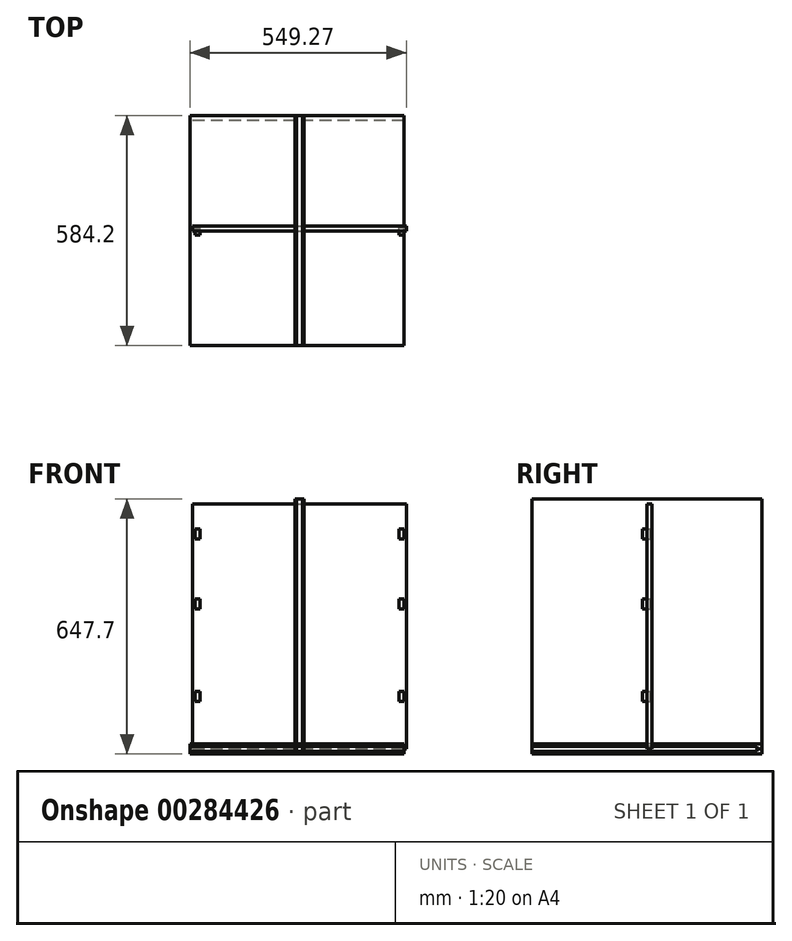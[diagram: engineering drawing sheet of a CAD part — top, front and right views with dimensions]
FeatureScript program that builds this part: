
annotation { "Feature Type Name" : "Feature", "Feature Type Description" : "" }
export const myFeature = defineFeature(function(context is Context, id is Id, definition is map)
    precondition{}
    {
        {
            assignVariable(context, id + "F0", {"name" : "Width", "anyValue" : 22.38});
        }
        {
            assignVariable(context, id + "F1", {"name" : "Height", "anyValue" : 25.5});
        }
        {
            assignVariable(context, id + "F2", {"name" : "Length", "anyValue" : 23});
        }
        {
            var Q0;
            Q0=qCreatedBy(makeId("Top.planeOp"),FACE);
            var sketch = newSketch(context, id + "F3", { "sketchPlane" : qUnion([Q0])});
            skLineSegment(sketch, "E0.bottom", {"start": v(277.81, 292.1) * mm, "end": v(-277.81, 292.1) * mm});
            skLineSegment(sketch, "E0.top", {"start": v(277.81, -292.1) * mm, "end": v(-277.81, -292.1) * mm});
            skLineSegment(sketch, "E0.left", {"start": v(277.81, 292.1) * mm, "end": v(277.81, -292.1) * mm});
            skLineSegment(sketch, "E0.right", {"start": v(-277.81, 292.1) * mm, "end": v(-277.81, -292.1) * mm});
            skPoint(sketch, "E0.middle", {"position": v(0, 0) * mm});
            skSolve(sketch);
        }
        {
            var Q0;
            Q0=makeQuery(id+"F3.imprint","IMPRINT",FACE,{"disambiguationData":[TD([[makeQuery(id+"F3.imprint","IMPRINT",EDGE,{"derivedFrom":sQuery(id+"F3.wireOp",EDGE,"E0.bottom")}),1.0]])]});
            extrude(context, id + "F4", {"entities" : qUnion([Q0]), "depth" : 19.05 * mm});
        }
        {
            var Q0;
            Q0=makeQuery(id+"F4.opExtrude","SWEPT_FACE",FACE,{"disambiguationData":[OSD([sQuery(id+"F3.wireOp",EDGE,"E0.right")])]});
            var sketch = newSketch(context, id + "F5", { "sketchPlane" : qUnion([Q0])});
            skLineSegment(sketch, "E1.bottom", {"start": v(-292.1, 19.05) * mm, "end": v(-279.4, 19.05) * mm});
            skLineSegment(sketch, "E1.top", {"start": v(-292.1, 12.7) * mm, "end": v(-279.4, 12.7) * mm});
            skLineSegment(sketch, "E1.left", {"start": v(-292.1, 19.05) * mm, "end": v(-292.1, 12.7) * mm});
            skLineSegment(sketch, "E1.right", {"start": v(-279.4, 19.05) * mm, "end": v(-279.4, 12.7) * mm});
            skSolve(sketch);
        }
        {
            var Q0;
            Q0 = qSketchRegion(id + "F5", true);
            extrude(context, id + "F6", {"entities" : qUnion([Q0]), "operationType" : NewBodyOperationType.REMOVE, "endBound" : BoundingType.THROUGH_ALL, "oppositeDirection" : true, "depth" : 25.4 * mm});
        }
        {
            var Q0;
            Q0=qCreatedBy(makeId("Right.planeOp"),FACE);
            cPlane(context, id + "F7", {"entities" : qUnion([Q0]), "cplaneType" : CPlaneType.OFFSET, "offset" : (getVariable(context, 'Width') / 2) * mm, "width" : 152.4 * mm, "height" : 152.4 * mm});
        }
        {
            var Q0;
            Q0=qCreatedBy(id+"F7.planeOp",FACE);
            var sketch = newSketch(context, id + "F8", { "sketchPlane" : qUnion([Q0])});
            skLineSegment(sketch, "E2.bottom", {"start": v(-292.1, 0) * mm, "end": v(292.1, 0) * mm});
            skLineSegment(sketch, "E2.top", {"start": v(-292.1, 647.7) * mm, "end": v(292.1, 647.7) * mm});
            skLineSegment(sketch, "E2.left", {"start": v(-292.1, 0) * mm, "end": v(-292.1, 647.7) * mm});
            skLineSegment(sketch, "E2.right", {"start": v(292.1, 0) * mm, "end": v(292.1, 647.7) * mm});
            skPoint(sketch, "E2.middle", {"position": v(0, 323.85) * mm});
            skSolve(sketch);
        }
        {
            var Q0;
            Q0 = qSketchRegion(id + "F8", true);
            extrude(context, id + "F9", {"entities" : qUnion([Q0]), "oppositeDirection" : true, "depth" : 19.05 * mm});
        }
        {
            var Q0;
            Q0=makeQuery(id+"F9.opExtrude","SWEPT_FACE",FACE,{"disambiguationData":[OSD([sQuery(id+"F8.wireOp",EDGE,"E2.top")])]});
            var sketch = newSketch(context, id + "F10", { "sketchPlane" : qUnion([Q0])});
            skLineSegment(sketch, "E3.bottom", {"start": v(265.11, 292.1) * mm, "end": v(271.46, 292.1) * mm});
            skLineSegment(sketch, "E3.top", {"start": v(265.11, 279.4) * mm, "end": v(271.46, 279.4) * mm});
            skLineSegment(sketch, "E3.left", {"start": v(265.11, 292.1) * mm, "end": v(265.11, 279.4) * mm});
            skLineSegment(sketch, "E3.right", {"start": v(271.46, 292.1) * mm, "end": v(271.46, 279.4) * mm});
            skSolve(sketch);
        }
        {
            var Q0;
            Q0=makeQuery(id+"F10.imprint","IMPRINT",FACE,{"disambiguationData":[TD([[makeQuery(id+"F10.imprint","IMPRINT",EDGE,{"derivedFrom":sQuery(id+"F10.wireOp",EDGE,"E3.bottom")}),-1.0]])]});
            extrude(context, id + "F11", {"entities" : qUnion([Q0]), "operationType" : NewBodyOperationType.REMOVE, "endBound" : BoundingType.THROUGH_ALL, "oppositeDirection" : true, "depth" : 25.4 * mm});
        }
        {
            var Q0;
            Q0=makeQuery(id+"F9.opExtrude","SWEPT_FACE",FACE,{"disambiguationData":[OSD([sQuery(id+"F8.wireOp",EDGE,"E2.left")])]});
            var sketch = newSketch(context, id + "F12", { "sketchPlane" : qUnion([Q0])});
            skLineSegment(sketch, "E4.bottom", {"start": v(265.11, 0) * mm, "end": v(277.81, 0) * mm});
            skLineSegment(sketch, "E4.top", {"start": v(265.11, 19.05) * mm, "end": v(277.81, 19.05) * mm});
            skLineSegment(sketch, "E4.left", {"start": v(265.11, 0) * mm, "end": v(265.11, 19.05) * mm});
            skLineSegment(sketch, "E4.right", {"start": v(277.81, 0) * mm, "end": v(277.81, 19.05) * mm});
            skLineSegment(sketch, "E5.bottom", {"start": v(265.11, 647.7) * mm, "end": v(277.81, 647.7) * mm});
            skLineSegment(sketch, "E5.top", {"start": v(265.11, 628.65) * mm, "end": v(277.81, 628.65) * mm});
            skLineSegment(sketch, "E5.left", {"start": v(265.11, 647.7) * mm, "end": v(265.11, 628.65) * mm});
            skLineSegment(sketch, "E5.right", {"start": v(277.81, 647.7) * mm, "end": v(277.81, 628.65) * mm});
            skSolve(sketch);
        }
        {
            var Q0;
            Q0 = qSketchRegion(id + "F12", true);
            extrude(context, id + "F13", {"entities" : qUnion([Q0]), "operationType" : NewBodyOperationType.REMOVE, "endBound" : BoundingType.THROUGH_ALL, "oppositeDirection" : true, "depth" : 25.4 * mm});
        }
        {
            var Q0;
            Q0=qCreatedBy(makeId("Front.planeOp"),FACE);
            cPlane(context, id + "F14", {"entities" : qUnion([Q0]), "cplaneType" : CPlaneType.OFFSET, "offset" : (getVariable(context, 'Length') / 2) * mm, "oppositeDirection" : true, "width" : 152.4 * mm, "height" : 152.4 * mm});
        }
        {
            var Q0;
            Q0=qCreatedBy(id+"F14.planeOp",FACE);
            var sketch = newSketch(context, id + "F15", { "sketchPlane" : qUnion([Q0])});
            skLineSegment(sketch, "E6.bottom", {"start": v(-271.46, 12.7) * mm, "end": v(271.46, 12.7) * mm});
            skLineSegment(sketch, "E6.top", {"start": v(-271.46, 635) * mm, "end": v(271.46, 635) * mm});
            skLineSegment(sketch, "E6.left", {"start": v(-271.46, 12.7) * mm, "end": v(-271.46, 635) * mm});
            skLineSegment(sketch, "E6.right", {"start": v(271.46, 12.7) * mm, "end": v(271.46, 635) * mm});
            skPoint(sketch, "E6.middle", {"position": v(0, 323.85) * mm});
            skSolve(sketch);
        }
        {
            var Q0;
            Q0=makeQuery(id+"F15.imprint","IMPRINT",FACE,{"disambiguationData":[TD([[makeQuery(id+"F15.imprint","IMPRINT",EDGE,{"derivedFrom":sQuery(id+"F15.wireOp",EDGE,"E6.bottom")}),1.0]])]});
            extrude(context, id + "F16", {"entities" : qUnion([Q0]), "depth" : 12.7 * mm});
        }
        {
            var Q0;
            Q0=qCreatedBy(makeId("Top.planeOp"),FACE);
            cPlane(context, id + "F17", {"entities" : qUnion([Q0]), "cplaneType" : CPlaneType.OFFSET, "offset" : (getVariable(context, 'Height') / 2) * mm, "width" : 152.4 * mm, "height" : 152.4 * mm});
        }
        {
            var Q0;
            Q0=makeQuery(id+"F4.opExtrude","SWEPT_BODY",BODY,{"disambiguationData":[OSD([sQuery(id+"F3.wireOp",EDGE,"E0.bottom"),sQuery(id+"F3.wireOp",EDGE,"E0.top"),sQuery(id+"F3.wireOp",EDGE,"E0.left"),sQuery(id+"F3.wireOp",EDGE,"E0.right")])]});
            var Q1;
            Q1=qCreatedBy(id+"F17.planeOp",FACE);
            mirror(context, id + "F18", {"entities" : qUnion([Q0]), "mirrorPlane" : qUnion([Q1])});
        }
        {
            var Q0;
            Q0=makeQuery(id+"F9.opExtrude","SWEPT_BODY",BODY,{"disambiguationData":[OSD([sQuery(id+"F8.wireOp",EDGE,"E2.bottom"),sQuery(id+"F8.wireOp",EDGE,"E2.top"),sQuery(id+"F8.wireOp",EDGE,"E2.left"),sQuery(id+"F8.wireOp",EDGE,"E2.right")])]});
            var Q1;
            Q1=qCreatedBy(makeId("Right.planeOp"),FACE);
            mirror(context, id + "F19", {"entities" : qUnion([Q0]), "mirrorPlane" : qUnion([Q1])});
        }
        {
            var Q0;
            Q0=qCreatedBy(makeId("Front.planeOp"),FACE);
            var sketch = newSketch(context, id + "F20", { "sketchPlane" : qUnion([Q0])});
            skLineSegment(sketch, "E7.bottom", {"start": v(265.11, 158.75) * mm, "end": v(252.41, 158.75) * mm});
            skLineSegment(sketch, "E7.top", {"start": v(265.11, 133.35) * mm, "end": v(252.41, 133.35) * mm});
            skLineSegment(sketch, "E7.left", {"start": v(265.11, 158.75) * mm, "end": v(265.11, 133.35) * mm});
            skLineSegment(sketch, "E7.right", {"start": v(252.41, 158.75) * mm, "end": v(252.41, 133.35) * mm});
            skLineSegment(sketch, "E8.bottom", {"start": v(265.11, 393.7) * mm, "end": v(252.41, 393.7) * mm});
            skLineSegment(sketch, "E8.top", {"start": v(265.11, 368.3) * mm, "end": v(252.41, 368.3) * mm});
            skLineSegment(sketch, "E8.left", {"start": v(265.11, 393.7) * mm, "end": v(265.11, 368.3) * mm});
            skLineSegment(sketch, "E8.right", {"start": v(252.41, 393.7) * mm, "end": v(252.41, 368.3) * mm});
            skLineSegment(sketch, "E9.bottom", {"start": v(265.11, 571.5) * mm, "end": v(252.41, 571.5) * mm});
            skLineSegment(sketch, "E9.top", {"start": v(265.11, 546.1) * mm, "end": v(252.41, 546.1) * mm});
            skLineSegment(sketch, "E9.left", {"start": v(265.11, 571.5) * mm, "end": v(265.11, 546.1) * mm});
            skLineSegment(sketch, "E9.right", {"start": v(252.41, 571.5) * mm, "end": v(252.41, 546.1) * mm});
            skPoint(sketch, "E10", {"position": v(265.11, 146.05) * mm});
            skPoint(sketch, "E11", {"position": v(265.11, 381) * mm});
            skPoint(sketch, "E12", {"position": v(265.11, 558.8) * mm});
            skSolve(sketch);
        }
        {
            var Q0;
            Q0 = qSketchRegion(id + "F20", true);
            extrude(context, id + "F21", {"entities" : qUnion([Q0]), "depth" : (getVariable(context, 'Length') / 2) * mm, "hasSecondDirection" : true, "secondDirectionOppositeDirection" : true, "secondDirectionDepth" : (18 - getVariable(context, 'Length') / 2) * mm});
        }
        {
            var Q0;
            Q0=makeQuery(id+"F21.opExtrude","SWEPT_BODY",BODY,{"disambiguationData":[OSD([sQuery(id+"F20.wireOp",EDGE,"E7.bottom"),sQuery(id+"F20.wireOp",EDGE,"E7.top"),sQuery(id+"F20.wireOp",EDGE,"E7.left"),sQuery(id+"F20.wireOp",EDGE,"E7.right")])]});
            var Q1;
            Q1=makeQuery(id+"F21.opExtrude","SWEPT_BODY",BODY,{"disambiguationData":[OSD([sQuery(id+"F20.wireOp",EDGE,"E8.bottom"),sQuery(id+"F20.wireOp",EDGE,"E8.top"),sQuery(id+"F20.wireOp",EDGE,"E8.left"),sQuery(id+"F20.wireOp",EDGE,"E8.right")])]});
            var Q2;
            Q2=makeQuery(id+"F21.opExtrude","SWEPT_BODY",BODY,{"disambiguationData":[OSD([sQuery(id+"F20.wireOp",EDGE,"E9.bottom"),sQuery(id+"F20.wireOp",EDGE,"E9.top"),sQuery(id+"F20.wireOp",EDGE,"E9.left"),sQuery(id+"F20.wireOp",EDGE,"E9.right")])]});
            var Q3;
            Q3=qCreatedBy(makeId("Right.planeOp"),FACE);
            mirror(context, id + "F22", {"entities" : qUnion([Q0, Q1, Q2]), "mirrorPlane" : qUnion([Q3])});
        }
    });
